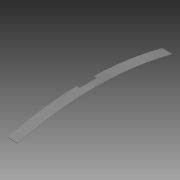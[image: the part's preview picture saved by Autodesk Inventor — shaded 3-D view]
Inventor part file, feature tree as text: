
AUTODESK INVENTOR PART (.ipt)
format: ipt  version: 2013 (Build 170138000, 138)  size: 121,344 bytes
history: native  units: in
note: dims shown in document units (in); Inventor stores cm internally (conversion verified against a paired STEP export)
features: extrude x2, plane x2, sketch x2, projected_geometry x1, other x1
ambient origin geometry x8: Origin, YZ Plane, XZ Plane, XY Plane, X Axis, Y Axis, Z Axis, Center Point
feature tree (8):
  extrude  "Extrusion5"  Depth=46.0in
  plane  "Work Plane2"
  extrude  "Extrusion6"  Depth=3.0in TaperAngle=0.0deg
  plane  "Work Plane3"
  sketch  "Sketch7"  dims[d2=0.125in d36=46.0in]
  sketch  "Sketch8"  dims[d37=0.125in d38=3.0in d39=0.0in d40=1.0in d41=5.0in d42=20.5in d43=20.5in d44=4.0in d45=0.0in d46=3.0in d47=23.0in d48=23.0in]
  projected_geometry  "Projected Loop3"
  other  "Definition1"
